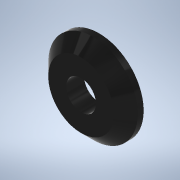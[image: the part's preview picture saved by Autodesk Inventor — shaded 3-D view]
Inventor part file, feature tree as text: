
AUTODESK INVENTOR PART (.ipt)
format: ipt  version: 2020 (Build 240168000, 168)  size: 110,080 bytes
history: native  units: mm
features: other x1, extrude x1, chamfer x1, sketch x1
ambient origin geometry x8: Origin, YZ Plane, XZ Plane, XY Plane, X Axis, Y Axis, Z Axis, Center Point
bodies: Body1 (feature_tree)
feature tree (4):
  other  "ソリッド1"
  extrude  "押し出し1"  Depth=15.0mm
  chamfer  "面取り1"  Distance=5.0mm
  sketch  "スケッチ1"
